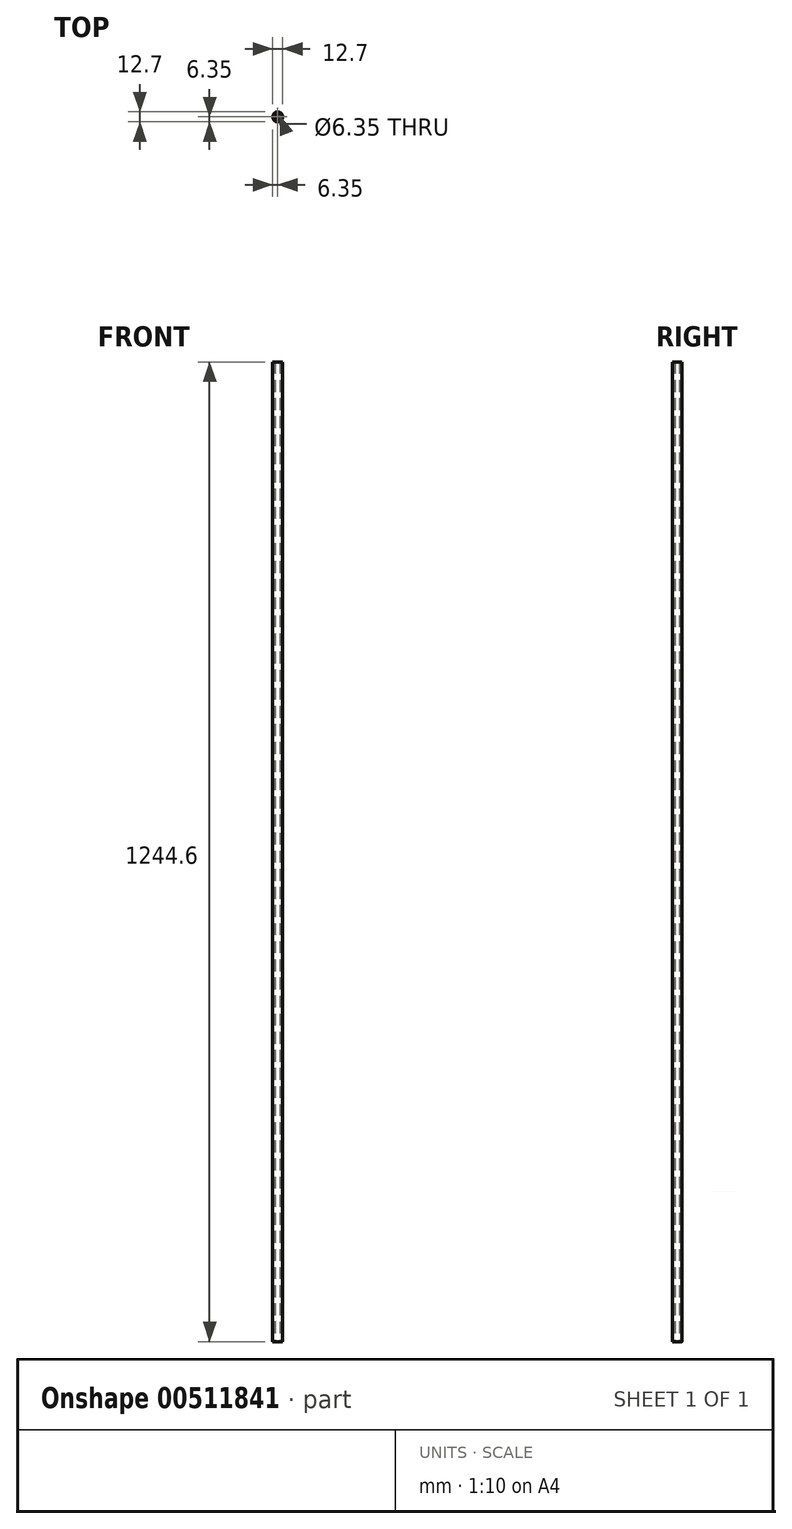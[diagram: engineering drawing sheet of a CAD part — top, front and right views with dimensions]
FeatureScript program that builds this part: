
annotation { "Feature Type Name" : "Feature", "Feature Type Description" : "" }
export const myFeature = defineFeature(function(context is Context, id is Id, definition is map)
    precondition{}
    {
        {
            var Q0;
            Q0=qCreatedBy(makeId("Top.planeOp"),FACE);
            var sketch = newSketch(context, id + "F0", { "sketchPlane" : qUnion([Q0])});
            skCircle(sketch, "E0", {"center": v(0, 0) * mm, "radius": 6.35 * mm});
            skSolve(sketch);
        }
        {
            var Q0;
            Q0=makeQuery(id+"F0.imprint","IMPRINT",FACE,{"disambiguationData":[TD([[makeQuery(id+"F0.imprint","IMPRINT",EDGE,{"derivedFrom":sQuery(id+"F0.wireOp",EDGE,"E0")}),1.0]])]});
            var Q1;
            Q1=sQuery(id+"F0.wireOp",EDGE,"E0");
            extrude(context, id + "F1", {"entities" : qUnion([Q0]), "surfaceEntities" : qUnion([Q1]), "depth" : 1244.6 * mm, "offsetDistance" : 25.4 * mm});
        }
        {
            var Q0;
            Q0=makeQuery(id+"F1.opExtrude","CAP_FACE",FACE,{"disambiguationData":[OSD([sQuery(id+"F0.wireOp",EDGE,"E0")])],"isStart":false});
            var Q1;
            Q1=makeQuery(id+"F1.opExtrude","CAP_FACE",FACE,{"disambiguationData":[OSD([sQuery(id+"F0.wireOp",EDGE,"E0")])],"isStart":true});
            shell(context, id + "F2", {"entities" : qUnion([Q0, Q1]), "thickness" : 3.17 * mm});
        }
    });
